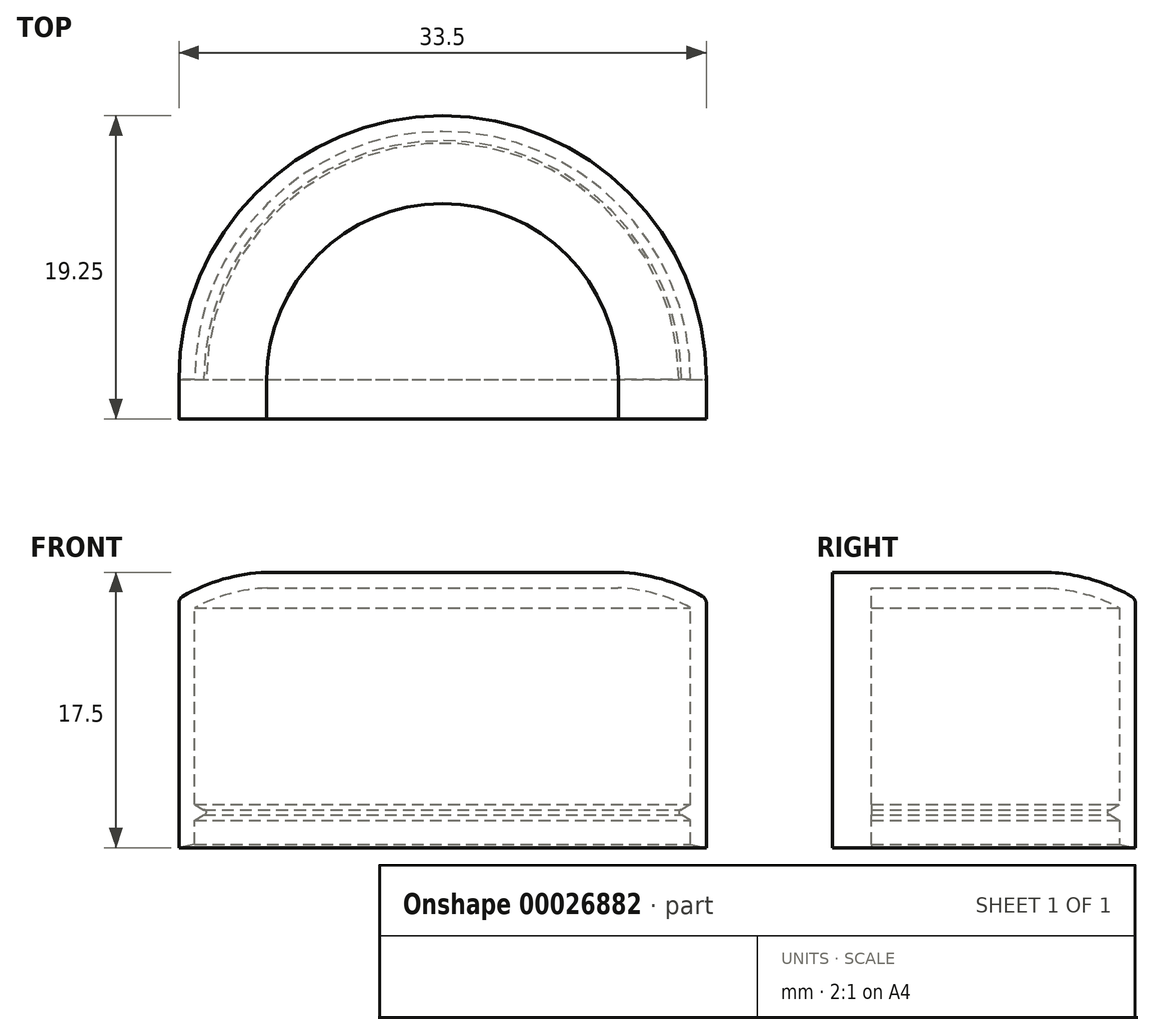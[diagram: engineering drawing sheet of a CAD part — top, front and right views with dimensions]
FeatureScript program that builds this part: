
annotation { "Feature Type Name" : "Feature", "Feature Type Description" : "" }
export const myFeature = defineFeature(function(context is Context, id is Id, definition is map)
    precondition{}
    {
        {
            var Q0;
            Q0=qCreatedBy(makeId("Front.planeOp"),FACE);
            var sketch = newSketch(context, id + "F0", { "sketchPlane" : qUnion([Q0])});
            skLineSegment(sketch, "E0", {"start": v(-13.4, 0) * mm, "end": v(25.4, 0) * mm, "construction": true});
            skLineSegment(sketch, "E1", {"start": v(0, -14.93) * mm, "end": v(0, 18.22) * mm, "construction": true});
            skLineSegment(sketch, "E2", {"start": v(16.75, 0) * mm, "end": v(16.75, 15.54) * mm});
            skLineSegment(sketch, "E3", {"start": v(11.17, 17.5) * mm, "end": v(0, 17.5) * mm});
            skArc(sketch, "E4", {"start": v(16.5, 15.97) * mm, "mid": v(13.93, 17.06) * mm, "end": v(11.17, 17.5) * mm});
            skPoint(sketch, "E5.newPointB", {"position": v(16.75, 17.5) * mm});
            skArc(sketch, "E5.filletArc", {"start": v(16.75, 15.54) * mm, "mid": v(16.68, 15.79) * mm, "end": v(16.5, 15.97) * mm});
            skLineSegment(sketch, "E6.0", {"start": v(11.15, 16.5) * mm, "end": v(0, 16.5) * mm});
            skArc(sketch, "E6.1", {"start": v(15.75, 15.24) * mm, "mid": v(13.52, 16.13) * mm, "end": v(11.15, 16.5) * mm});
            skLineSegment(sketch, "E6.2", {"start": v(15.75, 0.22) * mm, "end": v(15.75, 1.75) * mm});
            skLineSegment(sketch, "E7", {"start": v(0, 17.5) * mm, "end": v(0, 16.5) * mm});
            skLineSegment(sketch, "E8", {"start": v(15.75, 0.22) * mm, "end": v(16.75, 0) * mm});
            skArc(sketch, "E9", {"start": v(15.17, 2.42) * mm, "mid": v(15, 2.25) * mm, "end": v(15.17, 2.08) * mm});
            skLineSegment(sketch, "E10", {"start": v(15.75, 1.75) * mm, "end": v(15.17, 2.08) * mm});
            skLineSegment(sketch, "E11", {"start": v(15.75, 2.75) * mm, "end": v(15.17, 2.42) * mm});
            skLineSegment(sketch, "E12.trimOffspring", {"start": v(15.75, 2.75) * mm, "end": v(15.75, 15.24) * mm});
            skPoint(sketch, "E13.orphan", {"position": v(15.75, 2.25) * mm});
            skSolve(sketch);
        }
        {
            var Q0;
            Q0=makeQuery(id+"F0.imprint","IMPRINT",FACE,{"disambiguationData":[TD([[makeQuery(id+"F0.imprint","IMPRINT",EDGE,{"derivedFrom":sQuery(id+"F0.wireOp",EDGE,"E2")}),1.0]])]});
            var Q1;
            Q1=sQuery(id+"F0.wireOp",EDGE,"E1");
            revolve(context, id + "F1", {"entities" : qUnion([Q0]), "axis" : qUnion([Q1]), "revolveType" : RevolveType.ONE_DIRECTION, "angle" : 180 * degree});
        }
        {
            var Q0;
            Q0=qCreatedBy(makeId("Front.planeOp"),FACE);
            var sketch = newSketch(context, id + "F2", { "sketchPlane" : qUnion([Q0])});
            skLineSegment(sketch, "E14.0", {"start": v(16.75, 0) * mm, "end": v(16.75, 15.82) * mm});
            skArc(sketch, "E14.1", {"start": v(16.75, 15.82) * mm, "mid": v(14.07, 17.02) * mm, "end": v(11.17, 17.5) * mm});
            skLineSegment(sketch, "E14.2", {"start": v(-11.17, 17.5) * mm, "end": v(11.17, 17.5) * mm});
            skArc(sketch, "E14.3", {"start": v(-16.75, 15.82) * mm, "mid": v(-14.07, 17.02) * mm, "end": v(-11.17, 17.5) * mm});
            skLineSegment(sketch, "E14.4", {"start": v(-16.75, 0) * mm, "end": v(-16.75, 15.82) * mm});
            skLineSegment(sketch, "E15", {"start": v(-16.75, 0) * mm, "end": v(16.75, 0) * mm});
            skSolve(sketch);
        }
        {
            var Q0;
            Q0 = qSketchRegion(id + "F2", true);
            extrude(context, id + "F3", {"entities" : qUnion([Q0]), "operationType" : NewBodyOperationType.ADD, "depth" : 2.5 * mm});
        }
        {
            var Q0;
            Q0=makeQuery(id+"F3.opExtrude","SWEPT_EDGE",EDGE,{"disambiguationData":[OSD([sQuery(id+"F2.wireOp",EDGE,"E14.0"),sQuery(id+"F2.wireOp",EDGE,"E14.1")])]});
            var Q1;
            Q1=makeQuery(id+"F3.opExtrude","SWEPT_EDGE",EDGE,{"disambiguationData":[OSD([sQuery(id+"F2.wireOp",EDGE,"E14.3"),sQuery(id+"F2.wireOp",EDGE,"E14.4")])]});
            fillet(context, id + "F4", {"entities" : qUnion([Q0, Q1]), "radius" : 0.5 * mm, "tangentPropagation" : true, "allowEdgeOverflow" : false});
        }
    });
